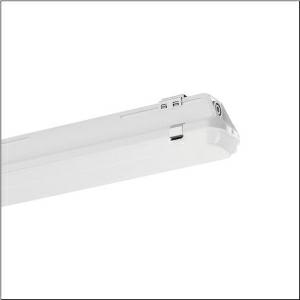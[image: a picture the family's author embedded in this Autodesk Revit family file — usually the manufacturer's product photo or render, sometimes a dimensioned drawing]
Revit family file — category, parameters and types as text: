
# Revit family: monsun_r__21_emergency_51fb207p467c3g_36ef
name_source: partatom
category: Lighting Fixtures
units: mm (PartAtom-declared; Revit-internal decimal feet)

## family parameters
Cut with Voids When Loaded = No
Host = Face
Light Source = No
Part Type = Normal
Room Calculation Point = No
Round Connector Dimension = Use Diameter
Shared = No

## types (1)
- --- (1 x LED, 820 lm, 7.1 W, 4000K)
    Apparent Load = 7 VA
    CIE Flux Codes = 45 75 93 94 100
    Color Rendering = 80
    Color Temperature = 4000K
    Default Elevation = 1800 mm
    Description = Monsun® 21 emergency, damp-proof luminaire, chain hanger, primary optical cover: enclosure, of PC, light emission: direct distribution, primary light characteristic: symmetric, installation type: suspended mounting, surface-mounted, horizontal mounting, vertical mounting, LED, rated luminous flux: 5.460lm, luminous efficacy: 160lm/W, light colour: 840, colour temperature: 4000K, control gear: ON/OFF, with terminal, 4-pole, max. 2.5mm², mains connection: 220..240V, AC, 50/60Hz, rated input power: 38W, control gear: single battery element, battery: LiFePO4, 9Ah, housing, of glass-fibre reinforced polyester, uncoated, bright grey, incl. chain hanger, length: 1.590mm, width: 90mm, height: 88mm, clip for enclosure, of stainless steel (V2A), ceiling mounting element, of stainless steel (V2A), chain hanger, of stainless steel (V2A), protection rating (complete): IP66, insulation class (complete): insulation class I (protective earthing), certification: CE, UKCA, protection symbol: D, impact resistance: IK08, permissible operating ambient temperature: +5..+25°C, standard: EN 50419, EN 60598-2-1, EN 60598-2-22, corresponds to IFS (International Featured Standards) requirements for safety and quality in the food industry, for indoor or canopied outdoor use, no direct snow, no direct sun, no direct rain, LABS conformity tested according to VDMA 24364:2018-05, contact your sales advisor before using the luminaires in applications with unclear chemical exposure, large temperature fluctuations or condensation-forming humidity, packaging unit: 1 piece
    Height = 89 mm
    Lamp = 1 x LED
    Lamp Light Flux = 820 lm
    Lamp Power = 7.1 W
    Lamp count = 1
    Length = 1590 mm
    Luminous efficacy = 115 lm/W
    Manufacturer = Siteco
    ModVariant = No
    Model = 51FB207P467C3G
    Mounting Place = Ceiling
    Mounting Type = Surface mounted
    Number of Poles = 1
    OnlyDefault = Yes
    Power Factor = 1
    Product Name = Monsun® 21 emergency
    Product group = damp-proof luminaire
    ProductGroupID = 300
    Protection Class = Protection class I
    Protection Degree = IP 66
    RLX_Detail_Level = 1
    RLX_Emergency_Light_Flux = 0 lm
    RLX_Emergency_Type = 0
    RLX_Emergency_Type_DB = No
    RlxData = <blob elided: 89125 chars, md5=fd780d5d>
    Socket = socket
    Standby Power = 0 W
    System Light Flux = 820 lm
    System Power = 7 W
    Type Comments = : emergency light operation: 3 h
    Type Image = l_1319656.jpg
    URL = http://relux.com
    VarID = @adj_041882
    Voltage = 0 V
    Weight = 0.00 kg
    Width = 90 mm

## geometry (parser evidence)
native form markers: Blend x4, Sweep x13
no freeform markers — native parametric forms only
